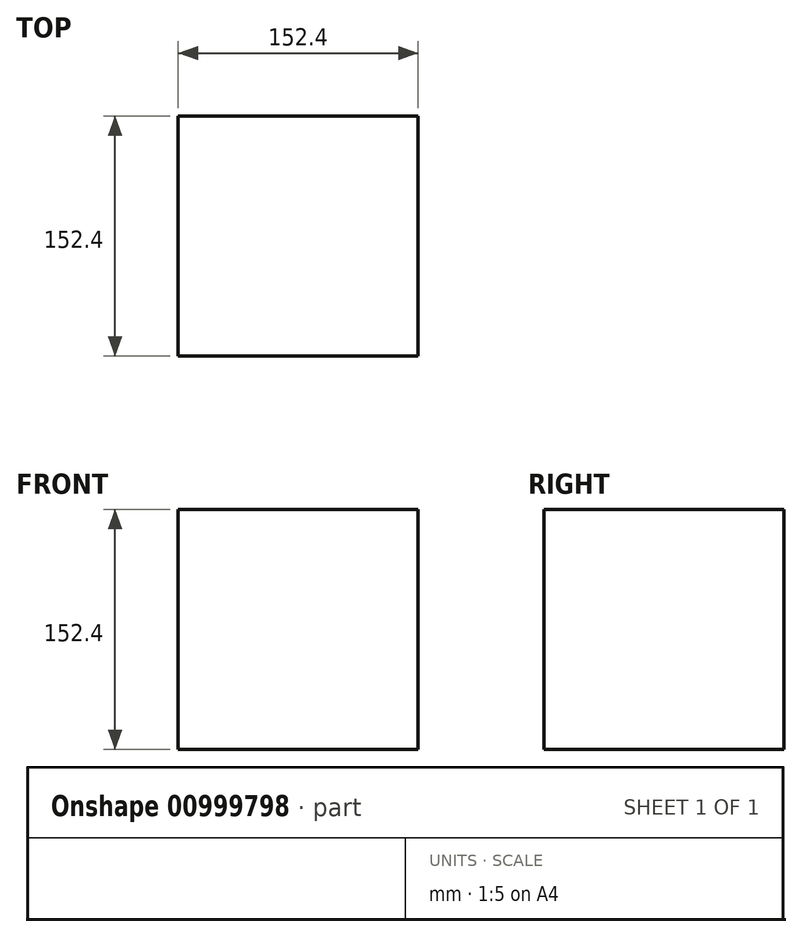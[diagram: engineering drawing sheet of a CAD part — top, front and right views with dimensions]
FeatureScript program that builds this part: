
annotation { "Feature Type Name" : "Feature", "Feature Type Description" : "" }
export const myFeature = defineFeature(function(context is Context, id is Id, definition is map)
    precondition{}
    {
        {
            assignVariable(context, id + "F0", {"variableType" : VariableType.LENGTH, "name" : "BoxDim", "lengthValue" : 152.4 * mm});
        }
        {
            var Q0;
            Q0=qCreatedBy(makeId("Right.planeOp"),FACE);
            var sketch = newSketch(context, id + "F1", { "sketchPlane" : qUnion([Q0])});
            skLineSegment(sketch, "E0.bottom", {"start": v(76.2, 76.2) * mm, "end": v(-76.2, 76.2) * mm});
            skLineSegment(sketch, "E0.top", {"start": v(76.2, -76.2) * mm, "end": v(-76.2, -76.2) * mm});
            skLineSegment(sketch, "E0.left", {"start": v(76.2, 76.2) * mm, "end": v(76.2, -76.2) * mm});
            skLineSegment(sketch, "E0.right", {"start": v(-76.2, 76.2) * mm, "end": v(-76.2, -76.2) * mm});
            skPoint(sketch, "E0.middle", {"position": v(0, 0) * mm});
            skSolve(sketch);
        }
        {
            var Q0;
            Q0=makeQuery(id+"F1.imprint","IMPRINT",FACE,{"disambiguationData":[TD([[makeQuery(id+"F1.imprint","IMPRINT",EDGE,{"derivedFrom":sQuery(id+"F1.wireOp",EDGE,"E0.bottom")}),1.0]])]});
            extrude(context, id + "F2", {"entities" : qUnion([Q0]), "depth" : getVariable(context, 'BoxDim'), "offsetDistance" : 25.4 * mm, "symmetric" : true});
        }
    });
